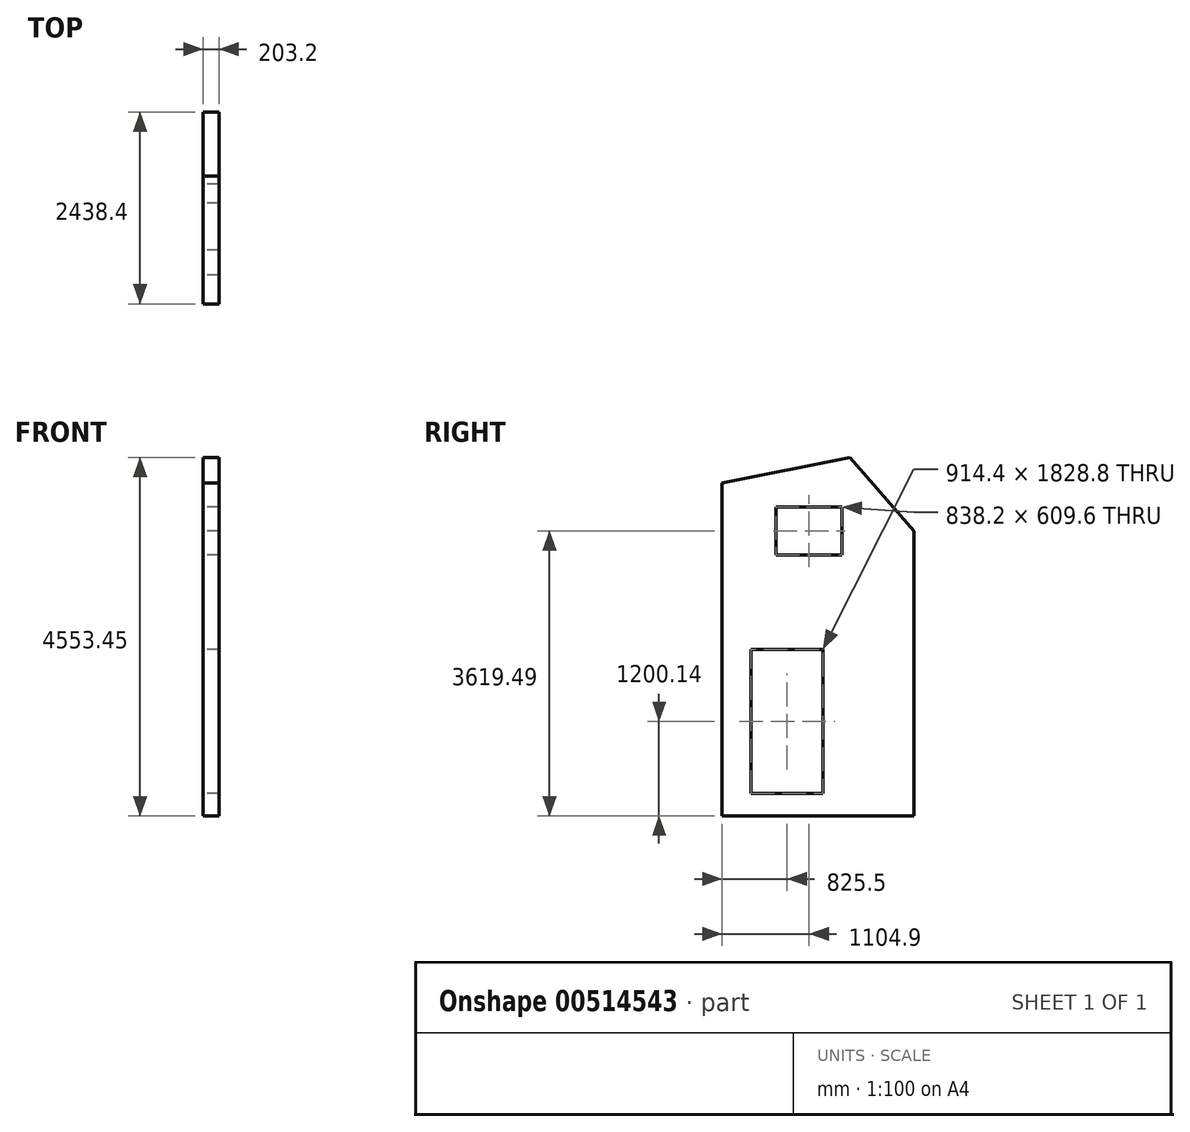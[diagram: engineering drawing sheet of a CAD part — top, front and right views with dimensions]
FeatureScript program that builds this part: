
annotation { "Feature Type Name" : "Feature", "Feature Type Description" : "" }
export const myFeature = defineFeature(function(context is Context, id is Id, definition is map)
    precondition{}
    {
        {
            var Q0;
            Q0=qCreatedBy(makeId("Right.planeOp"),FACE);
            var sketch = newSketch(context, id + "F0", { "sketchPlane" : qUnion([Q0])});
            skLineSegment(sketch, "E0.bottom", {"start": v(1061.08, 2363.14) * mm, "end": v(-1377.32, 2363.14) * mm});
            skLineSegment(sketch, "E0.top", {"start": v(1061.08, -2344.5) * mm, "end": v(-1377.32, -2344.5) * mm});
            skLineSegment(sketch, "E0.left", {"start": v(1061.08, 2363.14) * mm, "end": v(1061.08, -2344.5) * mm});
            skLineSegment(sketch, "E0.right", {"start": v(-1377.32, 2363.14) * mm, "end": v(-1377.32, -2344.5) * mm});
            skPoint(sketch, "E0.middle", {"position": v(-158.12, 9.32) * mm});
            skSolve(sketch);
        }
        {
            var Q0;
            Q0=makeQuery(id+"F0.imprint","IMPRINT",FACE,{"disambiguationData":[TD([[makeQuery(id+"F0.imprint","IMPRINT",EDGE,{"derivedFrom":sQuery(id+"F0.wireOp",EDGE,"E0.bottom")}),1.0]])]});
            extrude(context, id + "F1", {"entities" : qUnion([Q0]), "depth" : 203.2 * mm, "offsetDistance" : 25.4 * mm});
        }
        {
            var Q0;
            Q0=makeQuery(id+"F1.opExtrude","CAP_FACE",FACE,{"disambiguationData":[OSD([sQuery(id+"F0.wireOp",EDGE,"E0.bottom"),sQuery(id+"F0.wireOp",EDGE,"E0.top"),sQuery(id+"F0.wireOp",EDGE,"E0.left"),sQuery(id+"F0.wireOp",EDGE,"E0.right")])],"isStart":true});
            var sketch = newSketch(context, id + "F2", { "sketchPlane" : qUnion([Q0])});
            skLineSegment(sketch, "E1", {"start": v(-249.2, 2208.96) * mm, "end": v(-249.2, 55.8) * mm});
            skLineSegment(sketch, "E2", {"start": v(1377.32, 55.8) * mm, "end": v(1377.32, 1884.6) * mm});
            skLineSegment(sketch, "E3", {"start": v(-1061.08, 55.8) * mm, "end": v(-1061.08, 1275) * mm});
            skLineSegment(sketch, "E4", {"start": v(-1061.08, 55.8) * mm, "end": v(-249.2, 55.8) * mm});
            skLineSegment(sketch, "E5", {"start": v(-1061.08, 1275) * mm, "end": v(-249.2, 2208.96) * mm});
            skLineSegment(sketch, "E6", {"start": v(-1061.08, 1275) * mm, "end": v(-249.2, 1275) * mm});
            skLineSegment(sketch, "E7", {"start": v(1377.32, 1884.6) * mm, "end": v(-249.2, 2208.96) * mm});
            skLineSegment(sketch, "E8", {"start": v(-249.2, 2208.96) * mm, "end": v(-249.2, 2363.14) * mm});
            skLineSegment(sketch, "E9", {"start": v(1377.32, -2344.5) * mm, "end": v(1009.02, -2344.5) * mm});
            skLineSegment(sketch, "E10", {"start": v(1009.02, -2344.5) * mm, "end": v(1009.02, -2058.74) * mm});
            skLineSegment(sketch, "E11", {"start": v(94.62, -2058.74) * mm, "end": v(94.62, -2344.5) * mm});
            skLineSegment(sketch, "E12", {"start": v(94.62, -2058.74) * mm, "end": v(94.62, -229.94) * mm});
            skLineSegment(sketch, "E13", {"start": v(1009.02, -2058.74) * mm, "end": v(1009.02, -229.94) * mm});
            skLineSegment(sketch, "E14", {"start": v(94.62, -229.94) * mm, "end": v(1009.02, -229.94) * mm});
            skLineSegment(sketch, "E15", {"start": v(94.62, -2058.74) * mm, "end": v(1009.02, -2058.74) * mm});
            skLineSegment(sketch, "E16", {"start": v(1377.32, 1884.6) * mm, "end": v(-249.2, 1884.6) * mm});
            skSolve(sketch);
        }
        {
            var Q0;
            {var subQ0=sQuery(id+"F2.wireOp",EDGE,"E5");Q0=makeQuery(id+"F2.imprint","IMPRINT",FACE,{"disambiguationData":[TD([[makeQuery(id+"F2.imprint","IMPRINT",EDGE,{"derivedFrom":subQ0}),1.0]])]});}
            var Q1;
            {var subQ0=sQuery(id+"F2.wireOp",EDGE,"E7");Q1=makeQuery(id+"F2.imprint","IMPRINT",FACE,{"disambiguationData":[TD([[makeQuery(id+"F2.imprint","IMPRINT",EDGE,{"derivedFrom":subQ0}),-1.0]])]});}
            var Q2;
            Q2=makeQuery(id+"F2.imprint","IMPRINT",FACE,{"disambiguationData":[TD([[makeQuery(id+"F2.imprint","IMPRINT",EDGE,{"derivedFrom":sQuery(id+"F2.wireOp",EDGE,"E12")}),-1.0]])]});
            extrude(context, id + "F3", {"entities" : qUnion([Q0, Q1, Q2]), "operationType" : NewBodyOperationType.REMOVE, "oppositeDirection" : true, "depth" : 203.2 * mm, "offsetDistance" : 25.4 * mm});
        }
        {
            var Q0;
            Q0=makeQuery(id+"F1.opExtrude","CAP_FACE",FACE,{"disambiguationData":[OSD([sQuery(id+"F0.wireOp",EDGE,"E0.bottom"),sQuery(id+"F0.wireOp",EDGE,"E0.top"),sQuery(id+"F0.wireOp",EDGE,"E0.left"),sQuery(id+"F0.wireOp",EDGE,"E0.right")])],"isStart":true});
            var sketch = newSketch(context, id + "F4", { "sketchPlane" : qUnion([Q0])});
            skLineSegment(sketch, "E17", {"start": v(94.62, -229.94) * mm, "end": v(94.62, 55.8) * mm});
            skLineSegment(sketch, "E18", {"start": v(94.62, 55.8) * mm, "end": v(94.62, 970.2) * mm});
            skLineSegment(sketch, "E19.bottom", {"start": v(94.62, 970.2) * mm, "end": v(691.52, 970.2) * mm});
            skLineSegment(sketch, "E19.top", {"start": v(94.62, 1579.8) * mm, "end": v(691.52, 1579.8) * mm});
            skLineSegment(sketch, "E19.left", {"start": v(94.62, 970.2) * mm, "end": v(94.62, 1579.8) * mm});
            skLineSegment(sketch, "E19.right", {"start": v(691.52, 970.2) * mm, "end": v(691.52, 1579.8) * mm});
            skLineSegment(sketch, "E20.bottom", {"start": v(94.62, 1579.8) * mm, "end": v(-146.68, 1579.8) * mm});
            skLineSegment(sketch, "E20.top", {"start": v(94.62, 970.2) * mm, "end": v(-146.68, 970.2) * mm});
            skLineSegment(sketch, "E20.left", {"start": v(94.62, 1579.8) * mm, "end": v(94.62, 970.2) * mm});
            skLineSegment(sketch, "E20.right", {"start": v(-146.68, 1579.8) * mm, "end": v(-146.68, 970.2) * mm});
            skLineSegment(sketch, "E21", {"start": v(-1061.08, 1157.97) * mm, "end": v(-146.68, 1157.97) * mm});
            skLineSegment(sketch, "E22", {"start": v(-249.2, 2208.96) * mm, "end": v(-146.68, -2344.5) * mm});
            skLineSegment(sketch, "E23.0", {"start": v(1009.02, -2058.74) * mm, "end": v(1009.02, -229.94) * mm});
            skLineSegment(sketch, "E24.0", {"start": v(94.62, -229.94) * mm, "end": v(1009.02, -229.94) * mm});
            skSolve(sketch);
        }
        {
            var Q0;
            {var subQ1=sQuery(id+"F4.wireOp",EDGE,"E20.bottom");Q0=makeQuery(id+"F4.imprint","IMPRINT",FACE,{"disambiguationData":[TD([[makeQuery(id+"F4.imprint","IMPRINT",EDGE,{"derivedFrom":subQ1}),1.0]])]});}
            var Q1;
            Q1=makeQuery(id+"F4.imprint","IMPRINT",FACE,{"disambiguationData":[TD([[makeQuery(id+"F4.imprint","IMPRINT",EDGE,{"derivedFrom":sQuery(id+"F4.wireOp",EDGE,"E19.bottom")}),1.0]])]});
            extrude(context, id + "F5", {"entities" : qUnion([Q0, Q1]), "operationType" : NewBodyOperationType.REMOVE, "oppositeDirection" : true, "depth" : 203.2 * mm, "offsetDistance" : 25.4 * mm});
        }
    });
